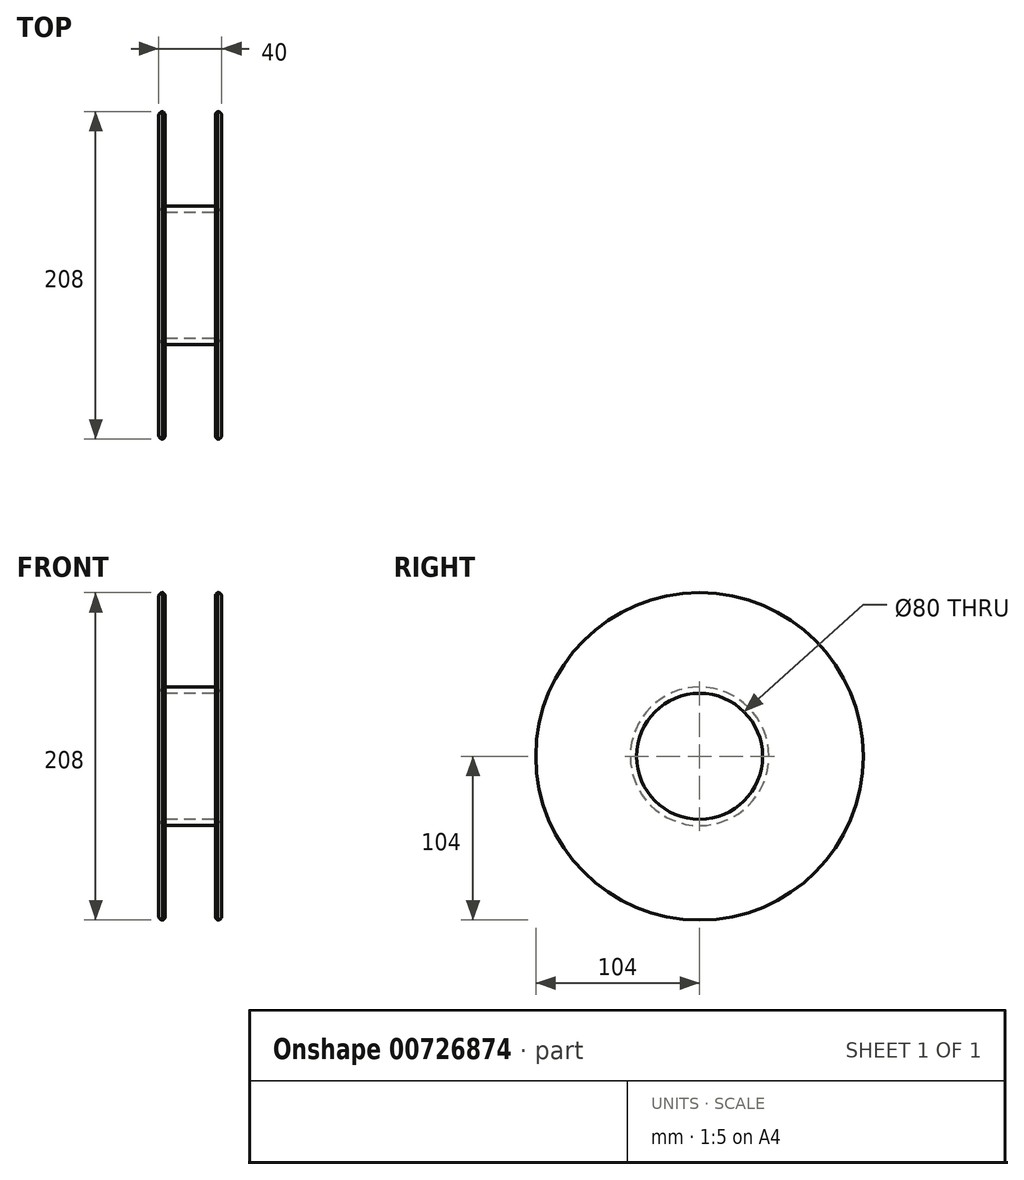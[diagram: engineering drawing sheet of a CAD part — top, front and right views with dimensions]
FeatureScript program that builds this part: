
annotation { "Feature Type Name" : "Feature", "Feature Type Description" : "" }
export const myFeature = defineFeature(function(context is Context, id is Id, definition is map)
    precondition{}
    {
        {
            var Q0;
            Q0=qCreatedBy(makeId("Front.planeOp"),FACE);
            var sketch = newSketch(context, id + "F0", { "sketchPlane" : qUnion([Q0])});
            skLineSegment(sketch, "E0", {"start": v(10, 40) * mm, "end": v(50, 40) * mm});
            skLineSegment(sketch, "E1", {"start": v(50, 40) * mm, "end": v(50, 44) * mm});
            skLineSegment(sketch, "E2", {"start": v(10, 44) * mm, "end": v(10, 40) * mm});
            skLineSegment(sketch, "E3", {"start": v(10, 44) * mm, "end": v(10, 104) * mm});
            skLineSegment(sketch, "E4", {"start": v(10, 104) * mm, "end": v(14, 104) * mm});
            skLineSegment(sketch, "E5", {"start": v(14, 104) * mm, "end": v(14, 44) * mm});
            skLineSegment(sketch, "E6", {"start": v(50, 44) * mm, "end": v(50, 104) * mm});
            skLineSegment(sketch, "E7", {"start": v(50, 104) * mm, "end": v(46, 104) * mm});
            skLineSegment(sketch, "E8", {"start": v(46, 104) * mm, "end": v(46, 44) * mm});
            skLineSegment(sketch, "E9", {"start": v(14, 44) * mm, "end": v(46, 44) * mm});
            skLineSegment(sketch, "E10", {"start": v(10, 40) * mm, "end": v(10, 0) * mm});
            skLineSegment(sketch, "E11", {"start": v(10, 0) * mm, "end": v(50, 0) * mm});
            skLineSegment(sketch, "E12", {"start": v(50, 0) * mm, "end": v(50, 40) * mm});
            skSolve(sketch);
        }
        {
            var Q0;
            Q0=makeQuery(id+"F0.imprint","IMPRINT",FACE,{"disambiguationData":[TD([[makeQuery(id+"F0.imprint","IMPRINT",EDGE,{"derivedFrom":sQuery(id+"F0.wireOp",EDGE,"E0")}),1.0]])]});
            var Q1;
            Q1=sQuery(id+"F0.wireOp",EDGE,"E11");
            revolve(context, id + "F1", {"surfaceOperationType" : NewSurfaceOperationType.NEW, "entities" : qUnion([Q0]), "axis" : qUnion([Q1]), "revolveType" : RevolveType.FULL});
        }
        {
            var Q0;
            Q0=makeQuery(id+"F1.opRevolve","SWEPT_EDGE",EDGE,{"disambiguationData":[OSD([sQuery(id+"F0.wireOp",EDGE,"E3"),sQuery(id+"F0.wireOp",EDGE,"E4")])]});
            var Q1;
            Q1=makeQuery(id+"F1.opRevolve","SWEPT_EDGE",EDGE,{"disambiguationData":[OSD([sQuery(id+"F0.wireOp",EDGE,"E6"),sQuery(id+"F0.wireOp",EDGE,"E7")])]});
            fillet(context, id + "F2", {"entities" : qUnion([Q0, Q1]), "radius" : 2.5 * mm, "tangentPropagation" : true, "allowEdgeOverflow" : false});
        }
        {
            var Q0;
            Q0=makeQuery(id+"F1.opRevolve","SWEPT_EDGE",EDGE,{"disambiguationData":[OSD([sQuery(id+"F0.wireOp",EDGE,"E4"),sQuery(id+"F0.wireOp",EDGE,"E5")])]});
            var Q1;
            Q1=makeQuery(id+"F1.opRevolve","SWEPT_EDGE",EDGE,{"disambiguationData":[OSD([sQuery(id+"F0.wireOp",EDGE,"E7"),sQuery(id+"F0.wireOp",EDGE,"E8")])]});
            fillet(context, id + "F3", {"entities" : qUnion([Q0, Q1]), "radius" : 2.5 * mm, "tangentPropagation" : true, "allowEdgeOverflow" : false});
        }
        {
            var Q0;
            Q0=makeQuery(id+"F1.opRevolve","SWEPT_EDGE",EDGE,{"disambiguationData":[OSD([sQuery(id+"F0.wireOp",EDGE,"E0"),sQuery(id+"F0.wireOp",EDGE,"E2"),sQuery(id+"F0.wireOp",EDGE,"E10")])]});
            fillet(context, id + "F4", {"entities" : qUnion([Q0]), "radius" : 5 * mm, "tangentPropagation" : true, "allowEdgeOverflow" : false});
        }
        {
            var Q0;
            Q0=makeQuery(id+"F1.opRevolve","SWEPT_EDGE",EDGE,{"disambiguationData":[OSD([sQuery(id+"F0.wireOp",EDGE,"E0"),sQuery(id+"F0.wireOp",EDGE,"E1"),sQuery(id+"F0.wireOp",EDGE,"E12")])]});
            fillet(context, id + "F5", {"entities" : qUnion([Q0]), "radius" : 5 * mm, "tangentPropagation" : true, "allowEdgeOverflow" : false});
        }
    });
